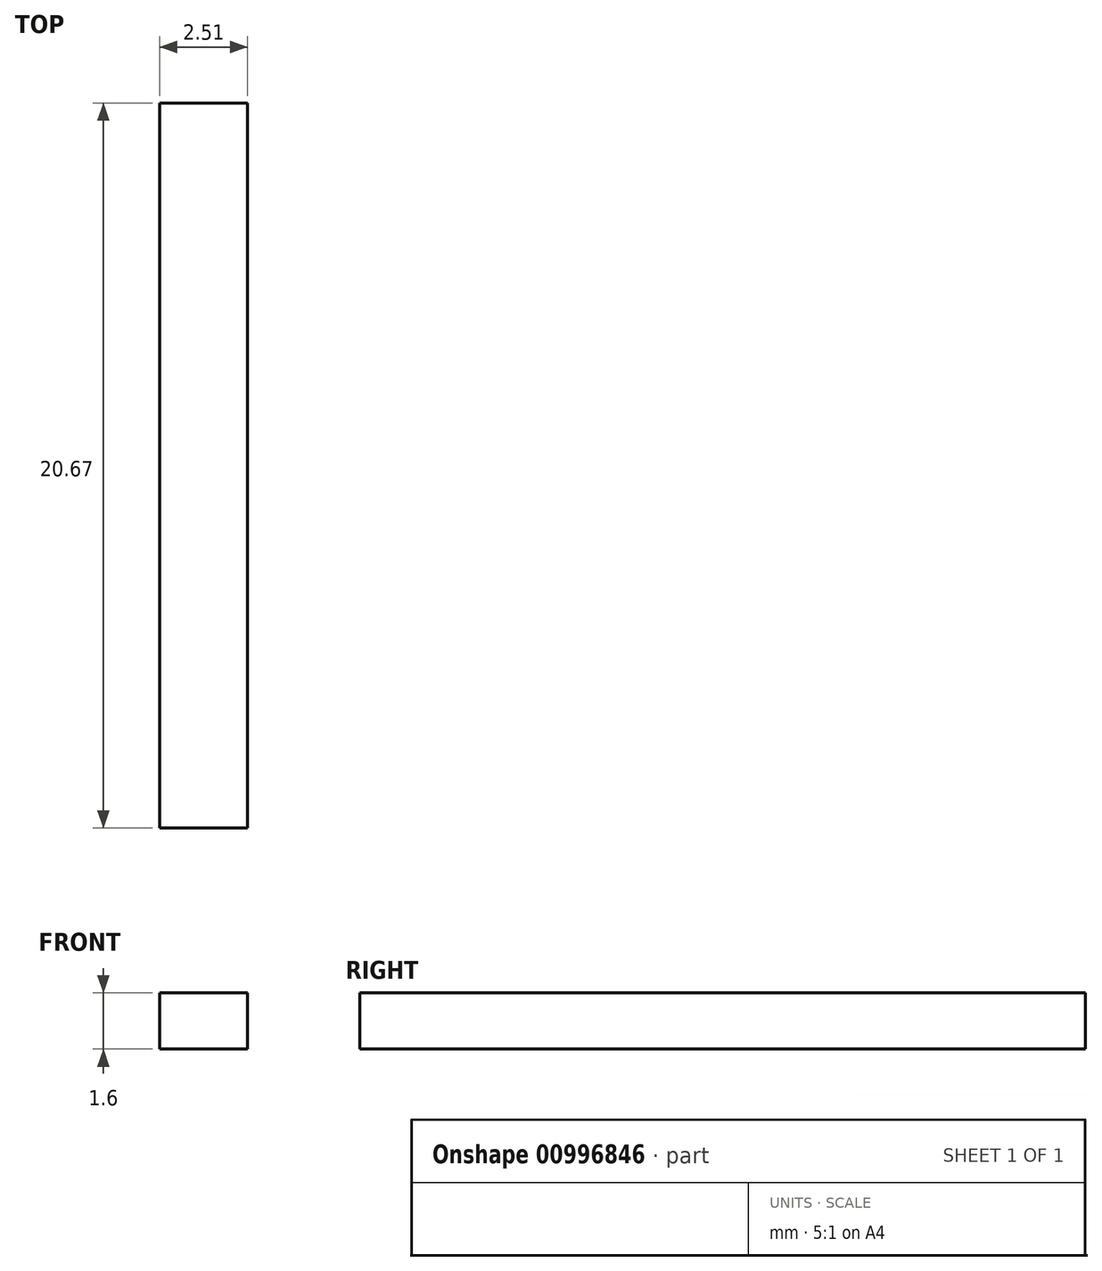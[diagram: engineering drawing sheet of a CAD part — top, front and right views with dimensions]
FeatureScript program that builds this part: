
annotation { "Feature Type Name" : "Feature", "Feature Type Description" : "" }
export const myFeature = defineFeature(function(context is Context, id is Id, definition is map)
    precondition{}
    {
        {
            var Q0;
            Q0=qCreatedBy(makeId("Top.planeOp"),FACE);
            var sketch = newSketch(context, id + "F0", { "sketchPlane" : qUnion([Q0])});
            skLineSegment(sketch, "E0.bottom", {"start": v(179.2, 0) * mm, "end": v(176.7, 0) * mm});
            skLineSegment(sketch, "E0.top", {"start": v(179.2, 20.67) * mm, "end": v(176.7, 20.67) * mm});
            skLineSegment(sketch, "E0.left", {"start": v(179.2, 0) * mm, "end": v(179.2, 20.67) * mm});
            skLineSegment(sketch, "E0.right", {"start": v(176.7, 0) * mm, "end": v(176.7, 20.67) * mm});
            skSolve(sketch);
        }
        {
            var Q0;
            Q0=makeQuery(id+"F0.imprint","IMPRINT",FACE,{"disambiguationData":[TD([[makeQuery(id+"F0.imprint","IMPRINT",EDGE,{"derivedFrom":sQuery(id+"F0.wireOp",EDGE,"E0.bottom")}),-1.0]])]});
            extrude(context, id + "F1", {"entities" : qUnion([Q0]), "depth" : 1.6 * mm, "offsetDistance" : 25 * mm});
        }
    });
